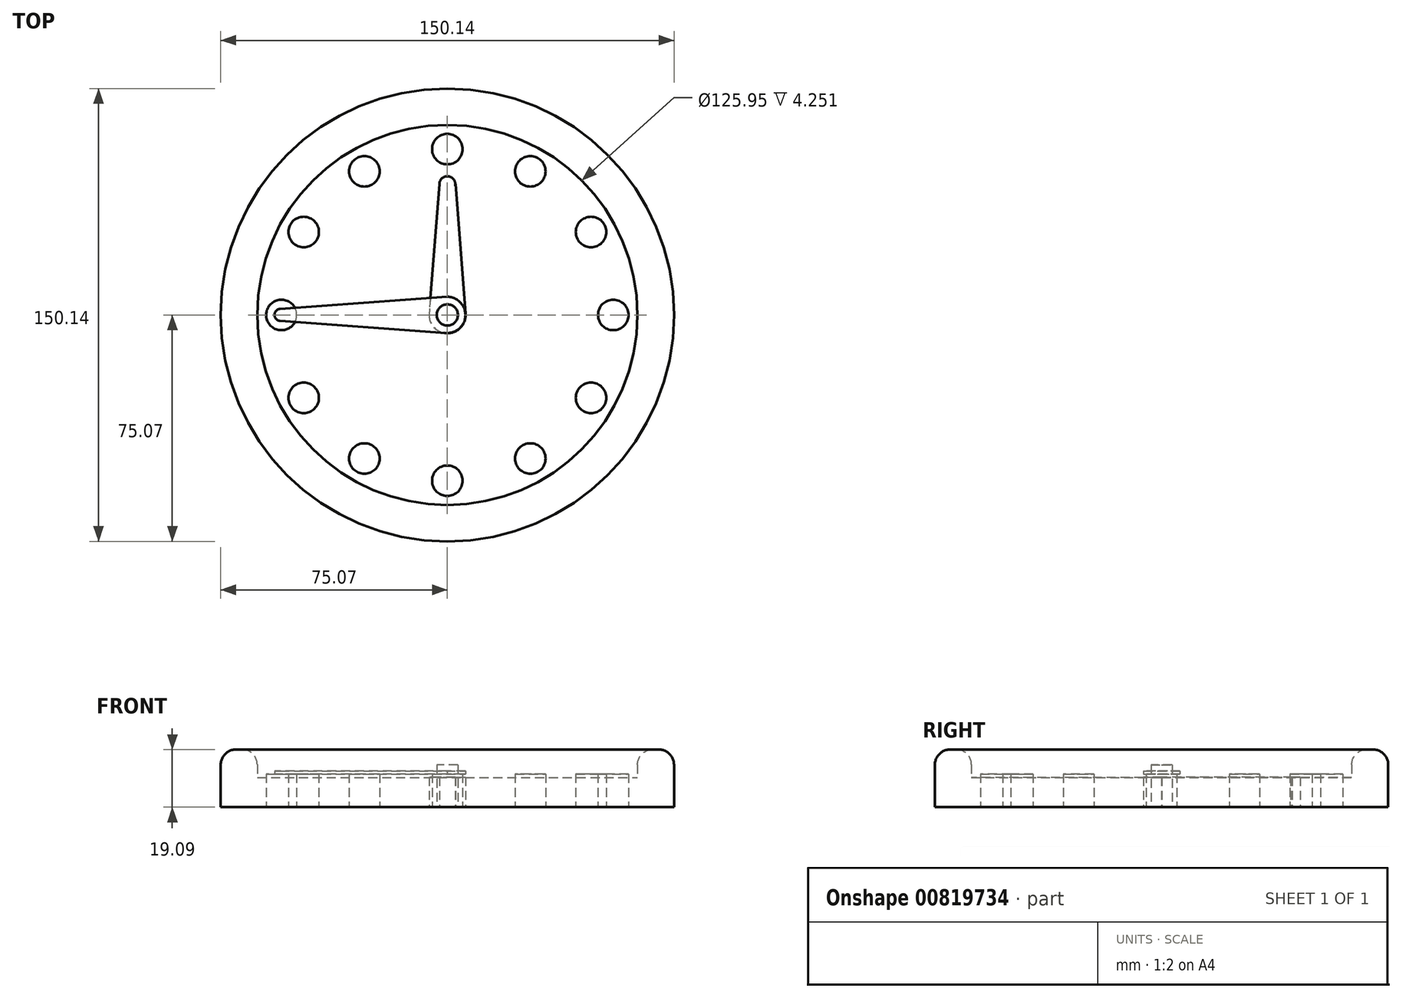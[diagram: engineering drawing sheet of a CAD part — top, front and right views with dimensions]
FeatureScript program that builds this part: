
annotation { "Feature Type Name" : "Feature", "Feature Type Description" : "" }
export const myFeature = defineFeature(function(context is Context, id is Id, definition is map)
    precondition{}
    {
        {
            var Q0;
            Q0=qCreatedBy(makeId("Front.planeOp"),FACE);
            var sketch = newSketch(context, id + "F0", { "sketchPlane" : qUnion([Q0])});
            skLineSegment(sketch, "E0", {"start": v(0, 0) * mm, "end": v(0, 59.66) * mm, "construction": true});
            skLineSegment(sketch, "E1.bottom", {"start": v(0, 0) * mm, "end": v(-75.07, 0) * mm});
            skLineSegment(sketch, "E1.top", {"start": v(0, 9.84) * mm, "end": v(-62.98, 9.84) * mm});
            skLineSegment(sketch, "E1.left", {"start": v(0, 0) * mm, "end": v(0, 9.84) * mm});
            skLineSegment(sketch, "E1.right", {"start": v(-75.07, 0) * mm, "end": v(-75.07, 9.84) * mm});
            skLineSegment(sketch, "E2.top", {"start": v(-70.07, 19.1) * mm, "end": v(-67.98, 19.1) * mm});
            skLineSegment(sketch, "E2.left", {"start": v(-75.07, 9.84) * mm, "end": v(-75.07, 14.1) * mm});
            skLineSegment(sketch, "E2.right", {"start": v(-62.98, 9.84) * mm, "end": v(-62.98, 14.1) * mm});
            skPoint(sketch, "E3.visualSharp", {"position": v(-75.07, 19.1) * mm});
            skArc(sketch, "E3.filletArc", {"start": v(-70.07, 19.1) * mm, "mid": v(-73.6, 17.63) * mm, "end": v(-75.07, 14.1) * mm});
            skPoint(sketch, "E4.visualSharp", {"position": v(-62.98, 19.1) * mm});
            skArc(sketch, "E4.filletArc", {"start": v(-62.98, 14.1) * mm, "mid": v(-64.44, 17.63) * mm, "end": v(-67.98, 19.1) * mm});
            skSolve(sketch);
        }
        {
            var Q0;
            Q0=makeQuery(id+"F0.imprint","IMPRINT",FACE,{"disambiguationData":[TD([[makeQuery(id+"F0.imprint","IMPRINT",EDGE,{"derivedFrom":sQuery(id+"F0.wireOp",EDGE,"E1.bottom")}),-1.0]])]});
            var Q1;
            Q1=sQuery(id+"F0.wireOp",EDGE,"E0");
            revolve(context, id + "F1", {"surfaceOperationType" : NewSurfaceOperationType.NEW, "entities" : qUnion([Q0]), "axis" : qUnion([Q1]), "revolveType" : RevolveType.FULL});
        }
        {
            var Q0;
            Q0=qCreatedBy(makeId("Top.planeOp"),FACE);
            var sketch = newSketch(context, id + "F2", { "sketchPlane" : qUnion([Q0])});
            skCircle(sketch, "E5", {"center": v(0, 55.44) * mm, "radius": 4.87 * mm});
            skCircle(sketch, "E6", {"center": v(57.02, 0) * mm, "radius": 4.67 * mm});
            skCircle(sketch, "E7", {"center": v(0, -54.97) * mm, "radius": 5.06 * mm});
            skCircle(sketch, "E8", {"center": v(-56.96, 0) * mm, "radius": 4.47 * mm});
            skCircle(sketch, "E9", {"center": v(24.25, 46.66) * mm, "radius": 5 * mm});
            skCircle(sketch, "E10", {"center": v(41.35, 28.14) * mm, "radius": 5.86 * mm});
            skCircle(sketch, "E11", {"center": v(46.57, -20.3) * mm, "radius": 6.37 * mm});
            skCircle(sketch, "E12", {"center": v(25.91, -41.2) * mm, "radius": 6.58 * mm});
            skCircle(sketch, "E13", {"center": v(-27.04, -41.2) * mm, "radius": 5.64 * mm});
            skCircle(sketch, "E14", {"center": v(-49.12, -20.06) * mm, "radius": 5.38 * mm});
            skCircle(sketch, "E15", {"center": v(-50.07, 23.39) * mm, "radius": 6.07 * mm});
            skCircle(sketch, "E16", {"center": v(-30.13, 45) * mm, "radius": 6.4 * mm});
            skSolve(sketch);
        }
        {
            var Q0;
            Q0=qCreatedBy(makeId("Front.planeOp"),FACE);
            var sketch = newSketch(context, id + "F3", { "sketchPlane" : qUnion([Q0])});
            skLineSegment(sketch, "E17", {"start": v(0, 0) * mm, "end": v(0, 39.53) * mm, "construction": true});
            skSolve(sketch);
        }
        {
            var Q0;
            Q0=makeQuery(id+"F2.imprint","IMPRINT",FACE,{"disambiguationData":[TD([[makeQuery(id+"F2.imprint","IMPRINT",EDGE,{"derivedFrom":sQuery(id+"F2.wireOp",EDGE,"E7")}),1.0]])]});
            extrude(context, id + "F4", {"entities" : qUnion([Q0]), "depth" : 11 * mm, "offsetDistance" : 25 * mm});
        }
        {
            var Q0;
            Q0=makeQuery(id+"F4.opExtrude","SWEPT_BODY",BODY,{"disambiguationData":[OSD([sQuery(id+"F2.wireOp",EDGE,"E7")])]});
            var Q1;
            Q1=sQuery(id+"F3.wireOp",EDGE,"E17");
            circularPattern(context, id + "F5", {"entities" : qUnion([Q0]), "axis" : qUnion([Q1]), "angle" : 360 * degree, "instanceCount" : 12, "equalSpace" : true});
        }
        {
            var Q0;
            Q0=qCreatedBy(makeId("Top.planeOp"),FACE);
            var sketch = newSketch(context, id + "F6", { "sketchPlane" : qUnion([Q0])});
            skCircle(sketch, "E18", {"center": v(0, 0) * mm, "radius": 3.5 * mm});
            skSolve(sketch);
        }
        {
            var Q0;
            Q0=makeQuery(id+"F6.imprint","IMPRINT",FACE,{"disambiguationData":[TD([[makeQuery(id+"F6.imprint","IMPRINT",EDGE,{"derivedFrom":sQuery(id+"F6.wireOp",EDGE,"E18")}),1.0]])]});
            var Q1;
            Q1=sQuery(id+"F6.wireOp",EDGE,"E18");
            extrude(context, id + "F7", {"entities" : qUnion([Q0]), "surfaceEntities" : qUnion([Q1]), "depth" : 14 * mm, "offsetDistance" : 25 * mm});
        }
        {
            var Q0;
            Q0=makeQuery(id+"F5.opPattern","COPY",FACE,{"derivedFrom":makeQuery(id+"F4.opExtrude","CAP_FACE",FACE,{"disambiguationData":[OSD([sQuery(id+"F2.wireOp",EDGE,"E7")])],"isStart":false}),"instanceName":"10"});
            var sketch = newSketch(context, id + "F8", { "sketchPlane" : qUnion([Q0])});
            skCircle(sketch, "E19", {"center": v(0, 0) * mm, "radius": 6 * mm});
            skLineSegment(sketch, "E20", {"start": v(0, 0) * mm, "end": v(-61.17, 0) * mm, "construction": true});
            skCircle(sketch, "E21", {"center": v(-55.24, 0) * mm, "radius": 2 * mm});
            skLineSegment(sketch, "E22", {"start": v(0, 6) * mm, "end": v(-55.38, 2) * mm});
            skLineSegment(sketch, "E23", {"start": v(-55.39, -2) * mm, "end": v(-0.43, -5.98) * mm});
            skSolve(sketch);
        }
        {
            var Q0;
            {var subQ0=sQuery(id+"F8.wireOp",EDGE,"E19");var subQ1=makeQuery(id+"F8.imprint","INTERSECT",VERTEX,{"derivedFrom":[subQ0,sQuery(id+"F8.wireOp",EDGE,"E23")]});Q0=makeQuery(id+"F8.imprint","IMPRINT",FACE,{"disambiguationData":[TD([[makeQuery(id+"F8.imprint","IMPRINT",EDGE,{"disambiguationData":[TD([[subQ1,1.0]])],"derivedFrom":subQ0}),1.0]])]});}
            var Q1;
            {var subQ0=sQuery(id+"F8.wireOp",EDGE,"E23");Q1=makeQuery(id+"F8.imprint","IMPRINT",FACE,{"disambiguationData":[TD([[makeQuery(id+"F8.imprint","IMPRINT",EDGE,{"derivedFrom":subQ0}),1.0]])]});}
            var Q2;
            {var subQ0=sQuery(id+"F8.wireOp",EDGE,"E21");var subQ1=makeQuery(id+"F8.imprint","INTERSECT",VERTEX,{"derivedFrom":[subQ0,sQuery(id+"F8.wireOp",EDGE,"E22")]});Q2=makeQuery(id+"F8.imprint","IMPRINT",FACE,{"disambiguationData":[TD([[makeQuery(id+"F8.imprint","IMPRINT",EDGE,{"disambiguationData":[TD([[subQ1,-1.0]])],"derivedFrom":subQ0}),1.0]])]});}
            extrude(context, id + "F9", {"entities" : qUnion([Q0, Q1, Q2]), "depth" : 1 * mm, "offsetDistance" : 25 * mm});
        }
        {
            var Q0;
            Q0=qCreatedBy(makeId("Top.planeOp"),FACE);
            var sketch = newSketch(context, id + "F10", { "sketchPlane" : qUnion([Q0])});
            skArc(sketch, "E24", {"start": v(-5.6, 2.26) * mm, "mid": v(-0.92, -5.98) * mm, "end": v(6.03, 0.47) * mm});
            skArc(sketch, "E25", {"start": v(2.58, 42.8) * mm, "mid": v(0.26, 45.95) * mm, "end": v(-2.64, 43.33) * mm});
            skLineSegment(sketch, "E26", {"start": v(-2.64, 43.33) * mm, "end": v(-6.07, 0) * mm});
            skLineSegment(sketch, "E27", {"start": v(-6.07, 0) * mm, "end": v(-5.6, 2.26) * mm});
            skLineSegment(sketch, "E28", {"start": v(2.69, 43.33) * mm, "end": v(6.06, 0) * mm});
            skLineSegment(sketch, "E29.trimOffspring", {"start": v(2.58, 42.8) * mm, "end": v(2.69, 43.33) * mm});
            skSolve(sketch);
        }
        {
            var Q0;
            Q0 = qSketchRegion(id + "F10", true);
            extrude(context, id + "F11", {"entities" : qUnion([Q0]), "depth" : 10 * mm, "offsetDistance" : 25 * mm});
        }
    });
